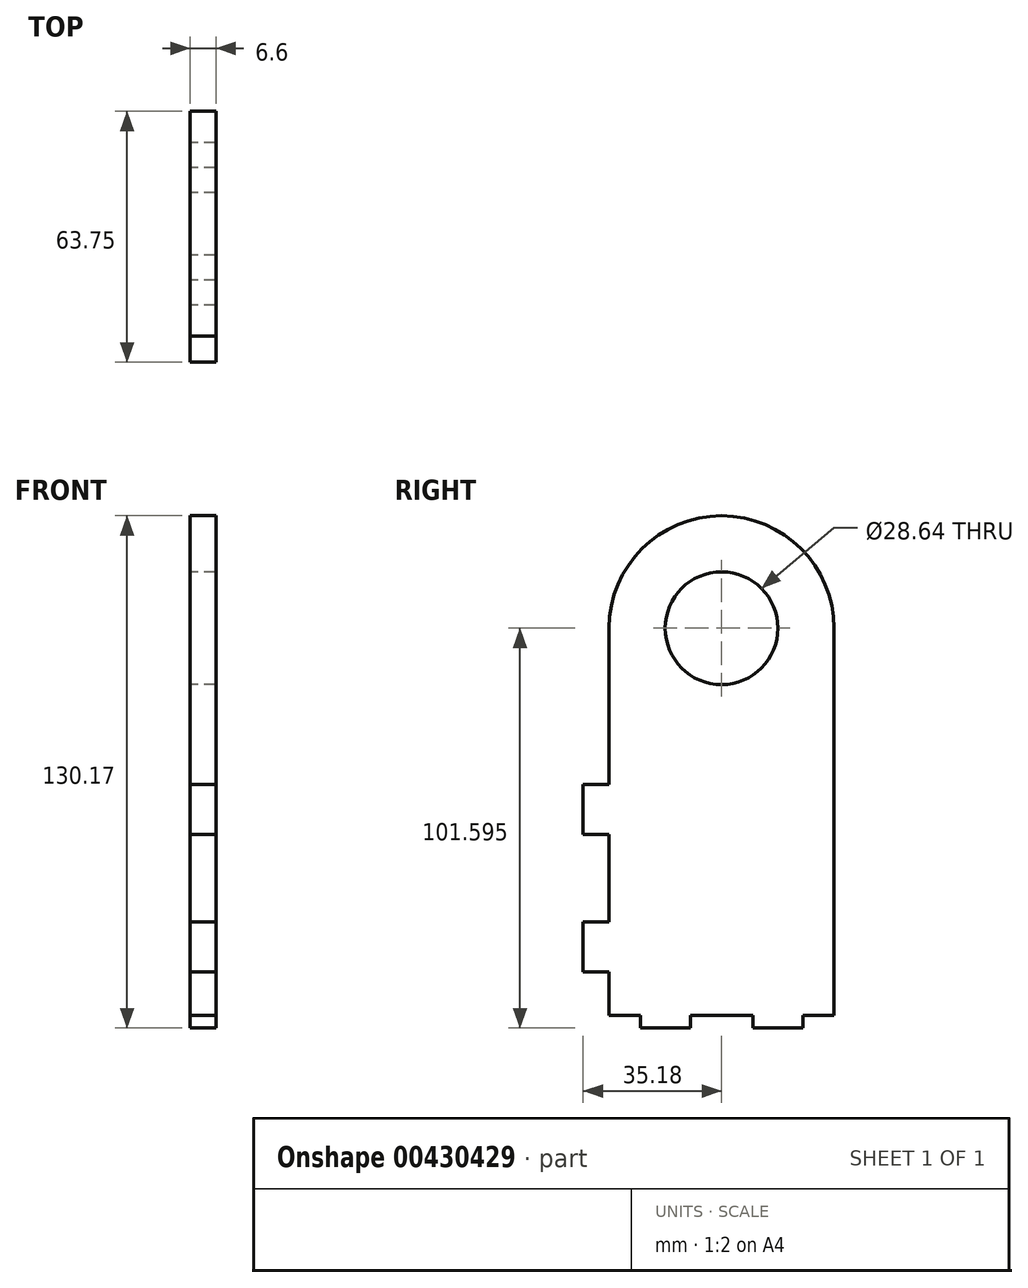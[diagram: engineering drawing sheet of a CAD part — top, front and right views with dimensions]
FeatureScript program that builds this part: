
annotation { "Feature Type Name" : "Feature", "Feature Type Description" : "" }
export const myFeature = defineFeature(function(context is Context, id is Id, definition is map)
    precondition{}
    {
        {
            var Q0;
            Q0=qCreatedBy(makeId("Right.planeOp"),FACE);
            cPlane(context, id + "F0", {"entities" : qUnion([Q0]), "cplaneType" : CPlaneType.OFFSET, "offset" : 101.6 * mm, "width" : 152.4 * mm, "height" : 152.4 * mm});
        }
        {
            var Q0;
            Q0=qCreatedBy(id+"F0.planeOp",FACE);
            var sketch = newSketch(context, id + "F1", { "sketchPlane" : qUnion([Q0])});
            skLineSegment(sketch, "E0.bottom", {"start": v(28.58, 69.85) * mm, "end": v(-28.57, 69.85) * mm});
            skLineSegment(sketch, "E0.top", {"start": v(28.57, 0) * mm, "end": v(-28.58, 0) * mm});
            skLineSegment(sketch, "E0.left", {"start": v(28.57, 69.85) * mm, "end": v(28.57, 0) * mm});
            skLineSegment(sketch, "E0.right", {"start": v(-28.57, 69.85) * mm, "end": v(-28.58, 0) * mm});
            skPoint(sketch, "E0.middle", {"position": v(0, 34.93) * mm});
            skCircle(sketch, "E1", {"center": v(0, 98.43) * mm, "radius": 28.58 * mm});
            skPoint(sketch, "E2", {"position": v(28.58, 98.43) * mm});
            skLineSegment(sketch, "E3", {"start": v(-28.57, 69.85) * mm, "end": v(-28.58, 98.42) * mm});
            skLineSegment(sketch, "E4", {"start": v(28.58, 98.43) * mm, "end": v(28.58, 69.85) * mm});
            skCircle(sketch, "E5", {"center": v(0, 98.43) * mm, "radius": 14.32 * mm});
            skPoint(sketch, "E6.endSnap0", {"position": v(28.57, 34.93) * mm});
            skLineSegment(sketch, "E7", {"start": v(-41.83, 34.93) * mm, "end": v(38.65, 34.93) * mm, "construction": true});
            skPoint(sketch, "E7.endSnap0", {"position": v(-28.58, 34.93) * mm});
            skLineSegment(sketch, "E8.bottom", {"start": v(-28.57, 46.04) * mm, "end": v(-35.18, 46.04) * mm});
            skLineSegment(sketch, "E8.top", {"start": v(-28.57, 58.74) * mm, "end": v(-35.18, 58.74) * mm});
            skLineSegment(sketch, "E8.left", {"start": v(-28.57, 46.04) * mm, "end": v(-28.57, 58.74) * mm});
            skLineSegment(sketch, "E8.right", {"start": v(-35.18, 46.04) * mm, "end": v(-35.18, 58.74) * mm});
            skLineSegment(sketch, "E9.MirrorCS", {"start": v(-28.57, 23.81) * mm, "end": v(-28.57, 11.11) * mm});
            skLineSegment(sketch, "E10.MirrorCS", {"start": v(-35.18, 23.81) * mm, "end": v(-35.18, 11.11) * mm});
            skLineSegment(sketch, "E11.MirrorCS", {"start": v(-28.57, 23.81) * mm, "end": v(-35.18, 23.81) * mm});
            skLineSegment(sketch, "E12.MirrorCS", {"start": v(-28.57, 11.11) * mm, "end": v(-35.18, 11.11) * mm});
            skLineSegment(sketch, "E13.bottom", {"start": v(-20.64, 0) * mm, "end": v(-7.94, 0) * mm});
            skLineSegment(sketch, "E13.top", {"start": v(-20.64, -3.18) * mm, "end": v(-7.94, -3.18) * mm});
            skLineSegment(sketch, "E13.left", {"start": v(-20.64, 0) * mm, "end": v(-20.64, -3.18) * mm});
            skLineSegment(sketch, "E13.right", {"start": v(-7.94, 0) * mm, "end": v(-7.94, -3.18) * mm});
            skLineSegment(sketch, "E14", {"start": v(0, 46.28) * mm, "end": v(0, 23.06) * mm, "construction": true});
            skLineSegment(sketch, "E15.MirrorCS", {"start": v(20.64, -3.18) * mm, "end": v(7.94, -3.18) * mm});
            skLineSegment(sketch, "E16.MirrorCS", {"start": v(7.94, 0) * mm, "end": v(7.94, -3.17) * mm});
            skLineSegment(sketch, "E17.MirrorCS", {"start": v(20.64, 0) * mm, "end": v(7.94, 0) * mm});
            skLineSegment(sketch, "E18.MirrorCS", {"start": v(20.64, 0) * mm, "end": v(20.64, -3.17) * mm});
            skSolve(sketch);
        }
        {
            var Q0;
            Q0 = qSketchRegion(id + "F1", true);
            extrude(context, id + "F2", {"entities" : qUnion([Q0]), "depth" : 6.6 * mm});
        }
    });
